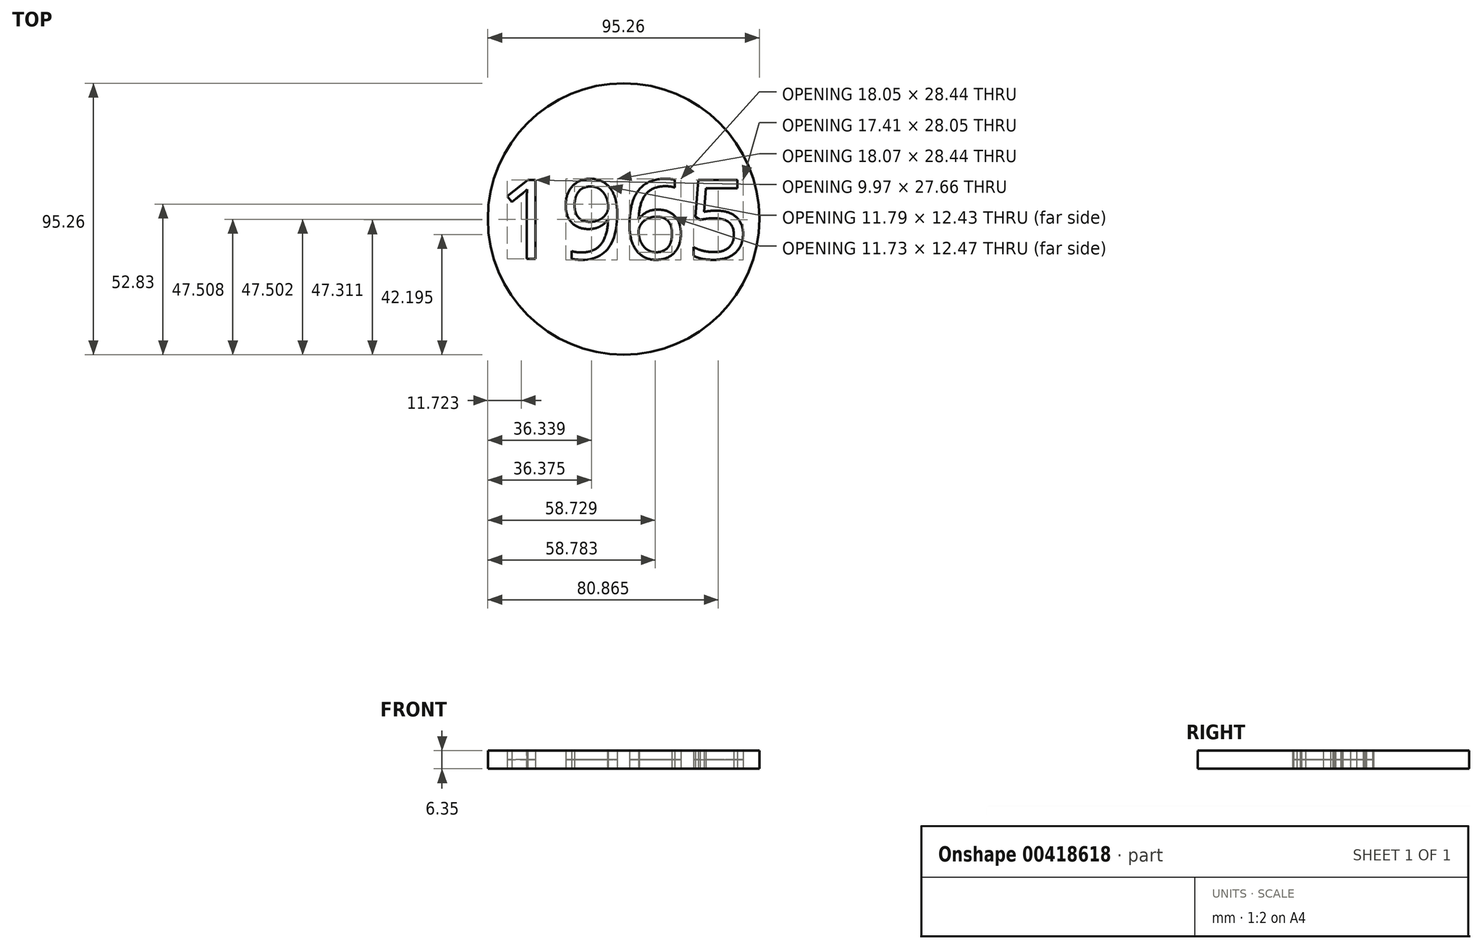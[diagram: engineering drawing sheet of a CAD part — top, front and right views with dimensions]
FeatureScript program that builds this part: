
annotation { "Feature Type Name" : "Feature", "Feature Type Description" : "" }
export const myFeature = defineFeature(function(context is Context, id is Id, definition is map)
    precondition{}
    {
        {
            var Q0;
            Q0=qCreatedBy(makeId("Top.planeOp"),FACE);
            var sketch = newSketch(context, id + "F0", { "sketchPlane" : qUnion([Q0])});
            skCircle(sketch, "E0", {"center": v(0, 0) * mm, "radius": 47.63 * mm});
            skText(sketch, "E1", { "text": "1965", "fontName": "OpenSans-Regular.ttf"});
            const initialGuessF0  = {"E1": [-0.04445, -0.01396, 1, 0, 0.0279]};
            skSetInitialGuess(sketch, initialGuessF0);
            skSolve(sketch);
        }
        {
            var Q0;
            Q0=makeQuery(id+"F0.imprint","IMPRINT",FACE,{"disambiguationData":[TD([[makeQuery(id+"F0.imprint","IMPRINT",EDGE,{"derivedFrom":sQuery(id+"F0.wireOp",EDGE,"E0")}),1.0]])]});
            var Q1;
            Q1=makeQuery(id+"F0.imprint","IMPRINT",FACE,{"disambiguationData":[TD([[makeQuery(id+"F0.imprint","IMPRINT",EDGE,{"derivedFrom":sQuery(id+"F0.wireOp",EDGE,"E1.sketch_text.stroke-25")}),1.0]])]});
            var Q2;
            Q2=makeQuery(id+"F0.imprint","IMPRINT",FACE,{"disambiguationData":[TD([[makeQuery(id+"F0.imprint","IMPRINT",EDGE,{"derivedFrom":sQuery(id+"F0.wireOp",EDGE,"E1.sketch_text.stroke-50")}),1.0]])]});
            extrude(context, id + "F1", {"entities" : qUnion([Q0, Q1, Q2]), "depth" : 6.35 * mm});
        }
        {
            var Q0;
            Q0=makeQuery(id+"F0.imprint","IMPRINT",FACE,{"disambiguationData":[TD([[makeQuery(id+"F0.imprint","IMPRINT",EDGE,{"derivedFrom":sQuery(id+"F0.wireOp",EDGE,"E1.sketch_text.stroke-0")}),-1.0]])]});
            var Q1;
            Q1=makeQuery(id+"F0.imprint","IMPRINT",FACE,{"disambiguationData":[TD([[makeQuery(id+"F0.imprint","IMPRINT",EDGE,{"derivedFrom":sQuery(id+"F0.wireOp",EDGE,"E1.sketch_text.stroke-9")}),-1.0]])]});
            var Q2;
            Q2=makeQuery(id+"F0.imprint","IMPRINT",FACE,{"disambiguationData":[TD([[makeQuery(id+"F0.imprint","IMPRINT",EDGE,{"derivedFrom":sQuery(id+"F0.wireOp",EDGE,"E1.sketch_text.stroke-35")}),-1.0]])]});
            var Q3;
            Q3=makeQuery(id+"F0.imprint","IMPRINT",FACE,{"disambiguationData":[TD([[makeQuery(id+"F0.imprint","IMPRINT",EDGE,{"derivedFrom":sQuery(id+"F0.wireOp",EDGE,"E1.sketch_text.stroke-60")}),-1.0]])]});
            extrude(context, id + "F2", {"entities" : qUnion([Q0, Q1, Q2, Q3]), "depth" : 3.17 * mm});
        }
    });
